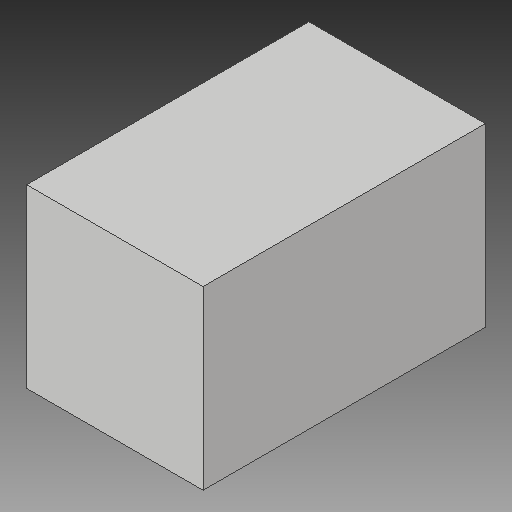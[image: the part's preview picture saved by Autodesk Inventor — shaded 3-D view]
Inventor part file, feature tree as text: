
AUTODESK INVENTOR PART (.ipt)
format: ipt  version: 2017 (Build 210142000, 142)  size: 82,944 bytes
history: native  units: in
note: dims shown in document units (in); Inventor stores cm internally (conversion verified against a paired STEP export)
features: extrude x1, sketch x1
ambient origin geometry x8: Origin, YZ Plane, XZ Plane, XY Plane, X Axis, Y Axis, Z Axis, Center Point
bodies: Solid1 (feature_tree)
feature tree (2):
  extrude  "Extrusion1"  Depth=1.25in
  sketch  "Sketch1"  dims[d0=1.25in d1=1.25in d2=2.0in d3=0.0in]
